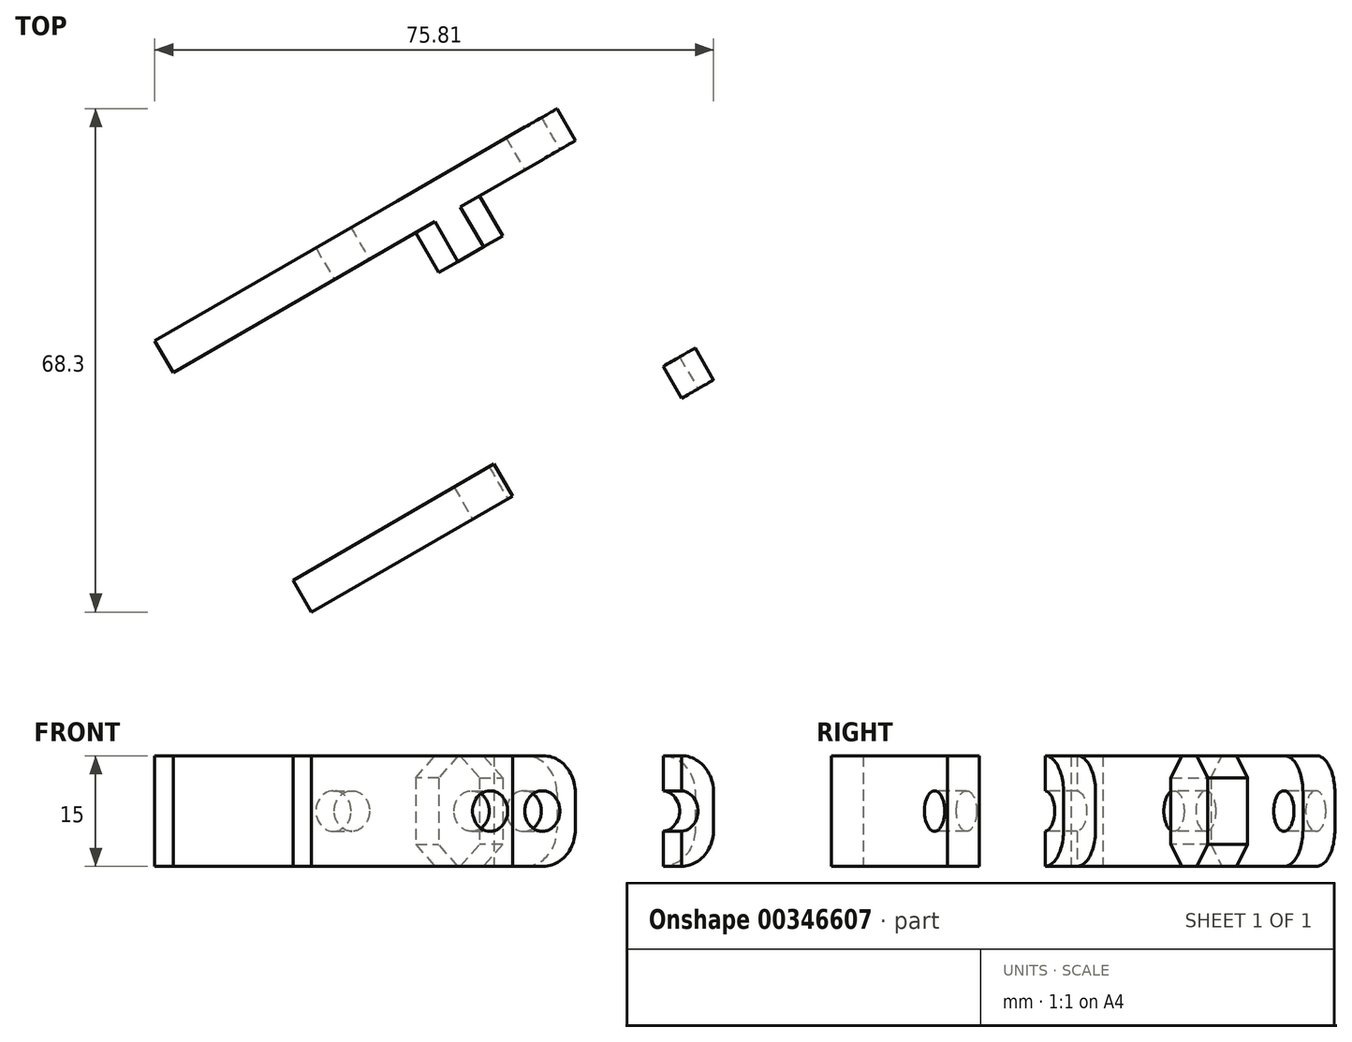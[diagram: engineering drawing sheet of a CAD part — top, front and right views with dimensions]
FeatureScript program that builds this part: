
annotation { "Feature Type Name" : "Feature", "Feature Type Description" : "" }
export const myFeature = defineFeature(function(context is Context, id is Id, definition is map)
    precondition{}
    {
        {
            var Q0;
            Q0=qCreatedBy(makeId("Top.planeOp"),FACE);
            var sketch = newSketch(context, id + "F0", { "sketchPlane" : qUnion([Q0])});
            skLineSegment(sketch, "E0", {"start": v(0, 0) * mm, "end": v(60, 0) * mm});
            skLineSegment(sketch, "E1", {"start": v(0, 0) * mm, "end": v(-60, 0) * mm});
            skLineSegment(sketch, "E2", {"start": v(-60, 0) * mm, "end": v(-90, 51.96) * mm});
            skLineSegment(sketch, "E3", {"start": v(-90, 51.96) * mm, "end": v(0, 103.92) * mm});
            skLineSegment(sketch, "E4", {"start": v(60, 0) * mm, "end": v(90, 51.96) * mm});
            skLineSegment(sketch, "E5", {"start": v(0, 103.92) * mm, "end": v(90, 51.96) * mm});
            skLineSegment(sketch, "E6", {"start": v(-87.8, 76.33) * mm, "end": v(-79.13, 81.33) * mm});
            skLineSegment(sketch, "E7", {"start": v(-68.8, 87.3) * mm, "end": v(-60.13, 92.3) * mm});
            skLineSegment(sketch, "E8", {"start": v(-100, 69.28) * mm, "end": v(-10, 121.24) * mm});
            skLineSegment(sketch, "E9", {"start": v(-100, 69.28) * mm, "end": v(-130, 121.24) * mm});
            skLineSegment(sketch, "E10", {"start": v(-130, 121.24) * mm, "end": v(-70, 225.17) * mm});
            skLineSegment(sketch, "E11", {"start": v(-70, 225.17) * mm, "end": v(-10, 225.17) * mm});
            skLineSegment(sketch, "E12", {"start": v(-10, 225.17) * mm, "end": v(-10, 121.24) * mm});
            skLineSegment(sketch, "E13", {"start": v(0, 0) * mm, "end": v(-52.5, 0) * mm});
            skLineSegment(sketch, "E14", {"start": v(-52.5, 0) * mm, "end": v(-78.75, 45.47) * mm});
            skLineSegment(sketch, "E15", {"start": v(0, 0) * mm, "end": v(52.5, 0) * mm});
            skLineSegment(sketch, "E16", {"start": v(52.5, 0) * mm, "end": v(78.75, 45.47) * mm});
            skLineSegment(sketch, "E17", {"start": v(78.75, 45.47) * mm, "end": v(0, 90.93) * mm});
            skLineSegment(sketch, "E18", {"start": v(0, 90.93) * mm, "end": v(-78.75, 45.47) * mm});
            skLineSegment(sketch, "E19", {"start": v(-100, 173.2) * mm, "end": v(-126.25, 127.74) * mm});
            skLineSegment(sketch, "E20", {"start": v(-100, 69.28) * mm, "end": v(-90, 51.96) * mm});
            skLineSegment(sketch, "E21", {"start": v(-126.25, 127.74) * mm, "end": v(-100, 82.27) * mm});
            skLineSegment(sketch, "E22", {"start": v(-100, 173.2) * mm, "end": v(-73.75, 218.67) * mm});
            skLineSegment(sketch, "E23", {"start": v(-73.75, 218.67) * mm, "end": v(-21.25, 218.67) * mm});
            skLineSegment(sketch, "E24", {"start": v(-21.25, 218.67) * mm, "end": v(-21.25, 127.74) * mm});
            skLineSegment(sketch, "E25", {"start": v(-21.25, 127.74) * mm, "end": v(-100, 82.27) * mm});
            skLineSegment(sketch, "E26", {"start": v(-100, 82.27) * mm, "end": v(-113, 74.77) * mm});
            skLineSegment(sketch, "E27", {"start": v(-113, 74.77) * mm, "end": v(-115.5, 79.1) * mm});
            skLineSegment(sketch, "E28", {"start": v(-115.5, 79.1) * mm, "end": v(-102.5, 86.6) * mm});
            skLineSegment(sketch, "E29", {"start": v(-78.75, 45.47) * mm, "end": v(-91.74, 37.97) * mm});
            skLineSegment(sketch, "E30", {"start": v(-91.74, 37.97) * mm, "end": v(-89.24, 33.64) * mm});
            skLineSegment(sketch, "E31", {"start": v(-89.24, 33.64) * mm, "end": v(-76.25, 41.14) * mm});
            skLineSegment(sketch, "E32", {"start": v(-91.74, 37.97) * mm, "end": v(-94.24, 42.3) * mm});
            skLineSegment(sketch, "E33", {"start": v(-94.24, 42.3) * mm, "end": v(-81.25, 49.8) * mm});
            skLineSegment(sketch, "E34", {"start": v(-113, 74.77) * mm, "end": v(-110.5, 70.44) * mm});
            skLineSegment(sketch, "E35", {"start": v(-110.5, 70.44) * mm, "end": v(-97.5, 77.94) * mm});
            skLineSegment(sketch, "E36", {"start": v(-97.5, 77.94) * mm, "end": v(-81.25, 49.8) * mm});
            skLineSegment(sketch, "E37", {"start": v(-78.75, 45.47) * mm, "end": v(-61.43, 55.47) * mm});
            skLineSegment(sketch, "E38", {"start": v(-61.43, 55.47) * mm, "end": v(-63.93, 59.8) * mm});
            skLineSegment(sketch, "E39", {"start": v(-63.93, 59.8) * mm, "end": v(-72.59, 54.8) * mm});
            skLineSegment(sketch, "E40", {"start": v(-72.59, 54.8) * mm, "end": v(-88.84, 82.94) * mm});
            skLineSegment(sketch, "E41", {"start": v(-88.84, 82.94) * mm, "end": v(-75.85, 90.44) * mm});
            skLineSegment(sketch, "E42", {"start": v(-75.85, 90.44) * mm, "end": v(-78.35, 94.77) * mm});
            skLineSegment(sketch, "E43", {"start": v(-63.93, 59.8) * mm, "end": v(-59.6, 62.3) * mm});
            skLineSegment(sketch, "E44", {"start": v(-59.6, 62.3) * mm, "end": v(-57.1, 57.97) * mm});
            skLineSegment(sketch, "E45", {"start": v(-57.1, 57.97) * mm, "end": v(-61.43, 55.47) * mm});
            skLineSegment(sketch, "E46", {"start": v(-113, 74.77) * mm, "end": v(-132.9, 63.27) * mm});
            skLineSegment(sketch, "E47", {"start": v(-91.74, 37.97) * mm, "end": v(-111.66, 26.47) * mm});
            skLineSegment(sketch, "E48", {"start": v(-111.66, 26.47) * mm, "end": v(-114.16, 30.8) * mm});
            skLineSegment(sketch, "E49", {"start": v(-114.16, 30.8) * mm, "end": v(-94.24, 42.3) * mm});
            skLineSegment(sketch, "E50", {"start": v(-132.9, 63.27) * mm, "end": v(-130.4, 58.94) * mm});
            skLineSegment(sketch, "E51", {"start": v(-130.4, 58.94) * mm, "end": v(-110.5, 70.44) * mm});
            skSolve(sketch);
        }
        {
            var Q0;
            {var subQ14=sQuery(id+"F0.wireOp",EDGE,"E41");Q0=makeQuery(id+"F0.imprint","IMPRINT",FACE,{"disambiguationData":[TD([[makeQuery(id+"F0.imprint","IMPRINT",EDGE,{"derivedFrom":subQ14}),1.0]])]});}
            var Q1;
            {var subQ5=sQuery(id+"F0.wireOp",EDGE,"E34");Q1=makeQuery(id+"F0.imprint","IMPRINT",FACE,{"disambiguationData":[TD([[makeQuery(id+"F0.imprint","IMPRINT",EDGE,{"derivedFrom":subQ5}),1.0]])]});}
            var Q2;
            {var subQ3=sQuery(id+"F0.wireOp",EDGE,"E8");var subQ7=makeQuery(id+"F0.imprint","IMPRINT",VERTEX,{"derivedFrom":subQ3});Q2=makeQuery(id+"F0.imprint","IMPRINT",FACE,{"disambiguationData":[TD([[makeQuery(id+"F0.imprint","IMPRINT",EDGE,{"disambiguationData":[TD([[subQ7,1.0]])],"derivedFrom":subQ3}),-1.0]])]});}
            var Q3;
            {var subQ0=sQuery(id+"F0.wireOp",EDGE,"E37");Q3=makeQuery(id+"F0.imprint","IMPRINT",FACE,{"disambiguationData":[TD([[makeQuery(id+"F0.imprint","IMPRINT",EDGE,{"derivedFrom":subQ0}),1.0]])]});}
            var Q4;
            {var subQ5=sQuery(id+"F0.wireOp",EDGE,"E32");Q4=makeQuery(id+"F0.imprint","IMPRINT",FACE,{"disambiguationData":[TD([[makeQuery(id+"F0.imprint","IMPRINT",EDGE,{"derivedFrom":subQ5}),-1.0]])]});}
            var Q5;
            Q5=makeQuery(id+"F0.imprint","IMPRINT",FACE,{"disambiguationData":[TD([[makeQuery(id+"F0.imprint","IMPRINT",EDGE,{"derivedFrom":sQuery(id+"F0.wireOp",EDGE,"E38")}),-1.0]])]});
            var Q6;
            Q6=makeQuery(id+"F0.imprint","IMPRINT",FACE,{"disambiguationData":[TD([[makeQuery(id+"F0.imprint","IMPRINT",EDGE,{"derivedFrom":sQuery(id+"F0.wireOp",EDGE,"E34")}),-1.0]])]});
            var Q7;
            Q7=makeQuery(id+"F0.imprint","IMPRINT",FACE,{"disambiguationData":[TD([[makeQuery(id+"F0.imprint","IMPRINT",EDGE,{"derivedFrom":sQuery(id+"F0.wireOp",EDGE,"E32")}),1.0]])]});
            extrude(context, id + "F1", {"entities" : qUnion([Q0, Q1, Q2, Q3, Q4, Q5, Q6, Q7]), "depth" : 15 * mm});
        }
        {
            var Q0;
            Q0=makeQuery(id+"F1.opExtrude","SWEPT_FACE",FACE,{"disambiguationData":[OSD([sQuery(id+"F0.wireOp",EDGE,"E29"),sQuery(id+"F0.wireOp",EDGE,"E37")])]});
            var sketch = newSketch(context, id + "F2", { "sketchPlane" : qUnion([Q0])});
            skLineSegment(sketch, "E52", {"start": v(-60.47, 7.5) * mm, "end": v(-55.47, 7.5) * mm});
            skCircle(sketch, "E53", {"center": v(-55.47, 7.5) * mm, "radius": 2.75 * mm});
            skLineSegment(sketch, "E54", {"start": v(-55.47, 7.5) * mm, "end": v(-25.65, 7.5) * mm});
            skCircle(sketch, "E55", {"center": v(-25.65, 7.5) * mm, "radius": 2.75 * mm});
            skSolve(sketch);
        }
        {
            var Q0;
            {var subQ0=sQuery(id+"F2.wireOp",EDGE,"E54");var subQ1=sQuery(id+"F2.wireOp",EDGE,"E52");var subQ2=makeQuery(id+"F2.imprint","INTERSECT",VERTEX,{"derivedFrom":[subQ1,subQ0]});Q0=makeQuery(id+"F2.imprint","IMPRINT",FACE,{"disambiguationData":[TD([[makeQuery(id+"F2.imprint","IMPRINT",EDGE,{"disambiguationData":[TD([[subQ2,1.0]])],"derivedFrom":subQ1}),1.0]])]});}
            var Q1;
            {var subQ0=sQuery(id+"F2.wireOp",EDGE,"E54");var subQ1=sQuery(id+"F2.wireOp",EDGE,"E52");var subQ2=makeQuery(id+"F2.imprint","INTERSECT",VERTEX,{"derivedFrom":[subQ1,subQ0]});Q1=makeQuery(id+"F2.imprint","IMPRINT",FACE,{"disambiguationData":[TD([[makeQuery(id+"F2.imprint","IMPRINT",EDGE,{"disambiguationData":[TD([[subQ2,1.0]])],"derivedFrom":subQ1}),-1.0]])]});}
            var Q2;
            Q2=makeQuery(id+"F2.imprint","IMPRINT",FACE,{"disambiguationData":[TD([[makeQuery(id+"F2.imprint","IMPRINT",EDGE,{"derivedFrom":sQuery(id+"F2.wireOp",EDGE,"E55")}),1.0]])]});
            extrude(context, id + "F3", {"entities" : qUnion([Q0, Q1, Q2]), "operationType" : NewBodyOperationType.REMOVE, "oppositeDirection" : true, "depth" : 60 * mm});
        }
        {
            var Q0;
            Q0=makeQuery(id+"F1.opExtrude","CAP_EDGE",EDGE,{"disambiguationData":[OSD([sQuery(id+"F0.wireOp",EDGE,"E36")])],"isStart":false});
            var Q1;
            Q1=makeQuery(id+"F1.opExtrude","CAP_EDGE",EDGE,{"disambiguationData":[OSD([sQuery(id+"F0.wireOp",EDGE,"E40")])],"isStart":false});
            var Q2;
            Q2=makeQuery(id+"F1.opExtrude","CAP_EDGE",EDGE,{"disambiguationData":[OSD([sQuery(id+"F0.wireOp",EDGE,"E36")])],"isStart":true});
            var Q3;
            Q3=makeQuery(id+"F1.opExtrude","CAP_EDGE",EDGE,{"disambiguationData":[OSD([sQuery(id+"F0.wireOp",EDGE,"E40")])],"isStart":true});
            chamfer(context, id + "F4", {"entities" : qUnion([Q0, Q1, Q2, Q3]), "width" : 3 * mm, "tangentPropagation" : true});
        }
        {
            var Q0;
            Q0=makeQuery(id+"F1.opExtrude","CAP_EDGE",EDGE,{"disambiguationData":[OSD([sQuery(id+"F0.wireOp",EDGE,"E32")])],"isStart":true});
            var Q1;
            Q1=makeQuery(id+"F1.opExtrude","CAP_EDGE",EDGE,{"disambiguationData":[OSD([sQuery(id+"F0.wireOp",EDGE,"E34")])],"isStart":true});
            var Q2;
            Q2=makeQuery(id+"F1.opExtrude","CAP_EDGE",EDGE,{"disambiguationData":[OSD([sQuery(id+"F0.wireOp",EDGE,"E34")])],"isStart":false});
            var Q3;
            Q3=makeQuery(id+"F1.opExtrude","CAP_EDGE",EDGE,{"disambiguationData":[OSD([sQuery(id+"F0.wireOp",EDGE,"E32")])],"isStart":false});
            var Q4;
            Q4=makeQuery(id+"F1.opExtrude","CAP_EDGE",EDGE,{"disambiguationData":[OSD([sQuery(id+"F0.wireOp",EDGE,"E44")])],"isStart":false});
            var Q5;
            Q5=makeQuery(id+"F1.opExtrude","CAP_EDGE",EDGE,{"disambiguationData":[OSD([sQuery(id+"F0.wireOp",EDGE,"E44")])],"isStart":true});
            var Q6;
            Q6=makeQuery(id+"F1.opExtrude","CAP_EDGE",EDGE,{"disambiguationData":[OSD([sQuery(id+"F0.wireOp",EDGE,"E42")])],"isStart":false});
            var Q7;
            Q7=makeQuery(id+"F1.opExtrude","CAP_EDGE",EDGE,{"disambiguationData":[OSD([sQuery(id+"F0.wireOp",EDGE,"E42")])],"isStart":true});
            fillet(context, id + "F5", {"entities" : qUnion([Q0, Q1, Q2, Q3, Q4, Q5, Q6, Q7]), "radius" : 5 * mm, "tangentPropagation" : true, "allowEdgeOverflow" : false});
        }
    });
